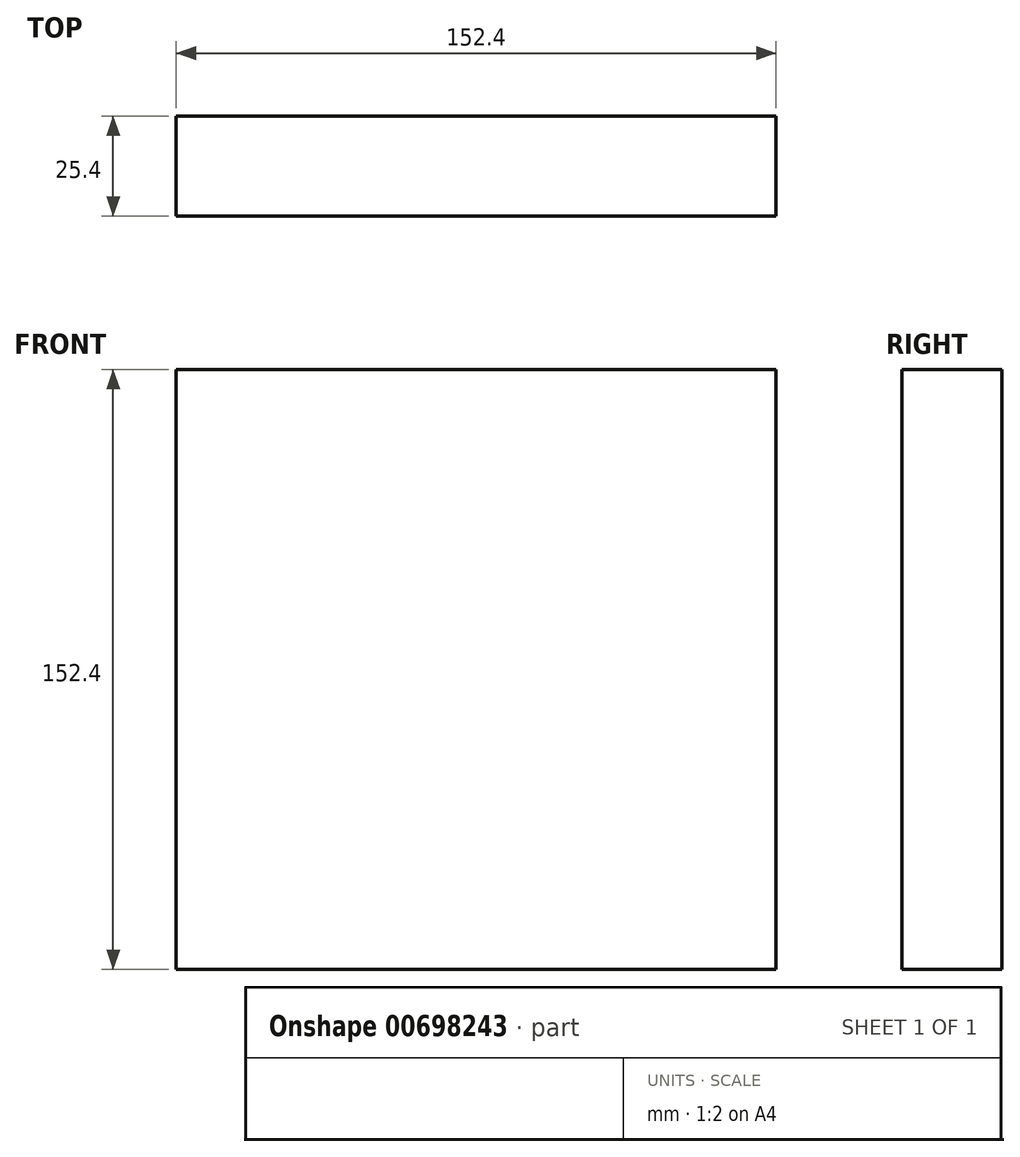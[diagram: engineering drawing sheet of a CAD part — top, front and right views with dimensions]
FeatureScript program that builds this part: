
annotation { "Feature Type Name" : "Feature", "Feature Type Description" : "" }
export const myFeature = defineFeature(function(context is Context, id is Id, definition is map)
    precondition{}
    {
        {
            var Q0;
            Q0=qCreatedBy(makeId("Front.planeOp"),FACE);
            var sketch = newSketch(context, id + "F0", { "sketchPlane" : qUnion([Q0])});
            skLineSegment(sketch, "E0.bottom", {"start": v(-82.52, 113) * mm, "end": v(69.88, 113) * mm});
            skLineSegment(sketch, "E0.top", {"start": v(-82.52, -39.4) * mm, "end": v(69.88, -39.4) * mm});
            skLineSegment(sketch, "E0.left", {"start": v(-82.52, 113) * mm, "end": v(-82.52, -39.4) * mm});
            skLineSegment(sketch, "E0.right", {"start": v(69.88, 113) * mm, "end": v(69.88, -39.4) * mm});
            skSolve(sketch);
        }
        {
            var Q0;
            Q0 = qSketchRegion(id + "F0", true);
            extrude(context, id + "F1", {"entities" : qUnion([Q0]), "depth" : 25.4 * mm, "offsetDistance" : 25.4 * mm});
        }
    });
